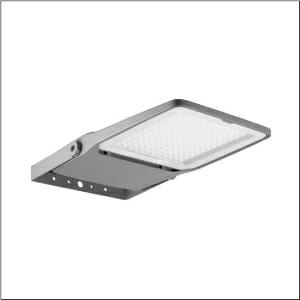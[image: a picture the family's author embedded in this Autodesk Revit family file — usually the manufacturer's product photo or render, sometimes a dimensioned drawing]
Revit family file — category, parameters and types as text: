
# Revit family: floodlight_fl_20_midi___pl61_5xa7682d2c2ac_159a
name_source: partatom
category: Lighting Fixtures
units: mm (PartAtom-declared; Revit-internal decimal feet)

## family parameters
Cut with Voids When Loaded = No
Host = Face
Light Source = No
Part Type = Normal
Room Calculation Point = No
Round Connector Dimension = Use Diameter
Shared = No

## types (1)
- --- (1 x LED 4000K / CRI = 70 (unbekannt), 18200 lm, 4000K)
    Apparent Load = 142 VA
    CIE Flux Codes = 33 65 98 100 100
    Color Rendering = 70
    Color Temperature = 4000K
    Default Elevation = 1800 mm
    Description = Floodlight FL 20 midi, floodlight, primary light control with lens, of plastic, primary optical cover: protective disc, of toughened safety glass, transparent, light distribution: PL61, light emission: direct distribution, primary light characteristic: asymmetric, installation type: surface-mounted, LED, High Power LED, rated luminous flux: 18.200lm, luminous efficacy: 128lm/W, light colour: 740, colour temperature: 4000K, control gear: ECG Plus, control: flexible luminous flux parameterisation, time-dependent luminous flux control, digital communication interface, power reduction, overheat protection, electronic power reduction, with terminal, 5-pole, max. 2.5mm², mains connection: 220..240V, AC, 50/60Hz, rated input power: 142W, LED unit, of diecast aluminium, powder-coated, Siteco® metallic grey (DB 702S), corrosivity category C5 mid according to DIN EN ISO 12944, incl. 1x M20 cable gland for cable Ø 6.5..12mm, length: 731mm, width: 450mm, height: 76mm, housing frame, of diecast aluminium, powder-coated, Siteco® metallic grey (DB 702S), wall fastening, of steel, powder-coated, Siteco® metallic grey (DB 702S), DALI, protection rating (complete): IP66, insulation class (complete): insulation class II (safety insulation), certification: CE, ENEC, VDE, protection symbol: D, permissible operating ambient temperature: -40..+40°C, permissible operating ambient temperature for outdoor applications: -40..+50°C, standard: DIN EN 12944, packaging unit: 1 piece

Light Distribution: PL61
    Height = 76 mm
    Lamp = 1 x LED 4000K / CRI >= 70 (unbekannt)
    Lamp Light Flux = 18200 lm
    Lamp count = 1
    Length = 731 mm
    Luminous efficacy = 128 lm/W
    Manufacturer = Siteco
    ModVariant = No
    Model = 5XA7682D2C2AC
    Mounting Place = Wall
    Mounting Type = Surface mounted
    Number of Poles = 1
    OnlyDefault = Yes
    Power Factor = 1
    Product Name = Floodlight FL 20 midi | PL61
    Product group = floodlight | wall mounted
    ProductGroupID = 2001
    Protection Class = Protection class II
    Protection Degree = IP 66
    RLX_Detail_Level = 1
    RLX_Emergency_Light_Flux = 0 lm
    RLX_Emergency_Type = 0
    RLX_Emergency_Type_DB = No
    RlxData = <blob elided: 92125 chars, md5=ab348c6d>
    Socket = socket
    Standby Power = 0 W
    System Light Flux = 18200 lm
    System Power = 142 W
    Type Comments = factory setting: luminous flux: 100 % | dim-lin: 254 | 489 mA
    Type Image = l_1005944.jpg
    URL = http://relux.com
    VarID = @adj_147243
    Voltage = 0 V
    Weight = 0.00 kg
    Width = 450 mm

## geometry (parser evidence)
native form markers: Blend x4, Sweep x12
no freeform markers — native parametric forms only
